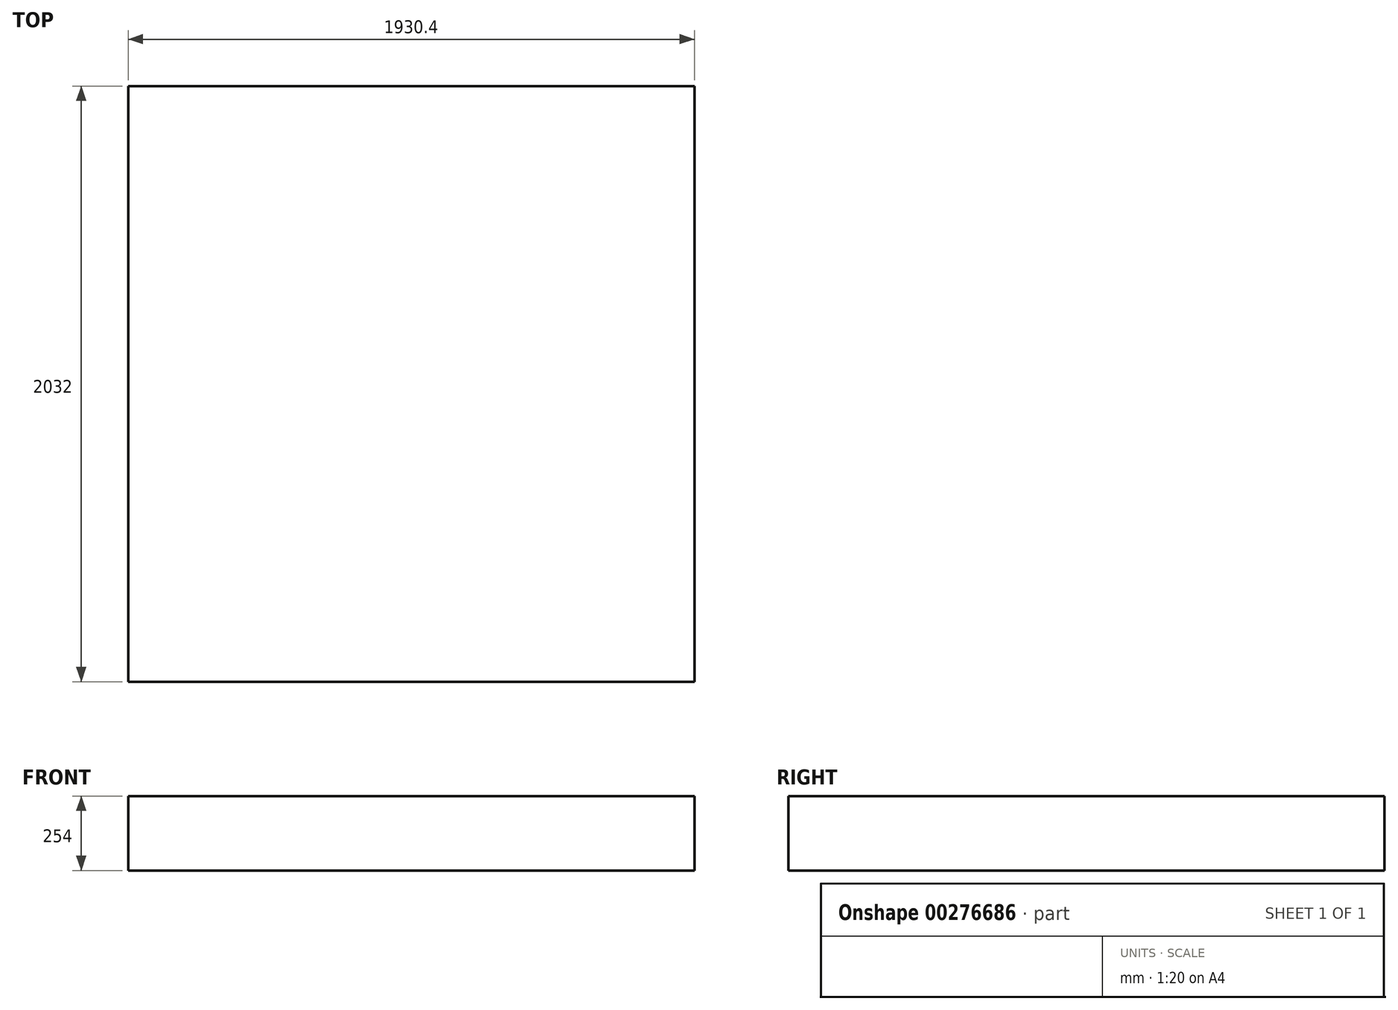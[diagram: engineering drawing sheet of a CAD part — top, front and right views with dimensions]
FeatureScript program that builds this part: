
annotation { "Feature Type Name" : "Feature", "Feature Type Description" : "" }
export const myFeature = defineFeature(function(context is Context, id is Id, definition is map)
    precondition{}
    {
        {
            var Q0;
            Q0=qCreatedBy(makeId("Top.planeOp"),FACE);
            var sketch = newSketch(context, id + "F0", { "sketchPlane" : qUnion([Q0])});
            skLineSegment(sketch, "E0.bottom", {"start": v(979.69, -1126.92) * mm, "end": v(-950.71, -1126.92) * mm});
            skLineSegment(sketch, "E0.top", {"start": v(979.69, 905.08) * mm, "end": v(-950.71, 905.08) * mm});
            skLineSegment(sketch, "E0.left", {"start": v(979.69, -1126.92) * mm, "end": v(979.69, 905.08) * mm});
            skLineSegment(sketch, "E0.right", {"start": v(-950.71, -1126.92) * mm, "end": v(-950.71, 905.08) * mm});
            skSolve(sketch);
        }
        {
            var Q0;
            Q0=makeQuery(id+"F0.imprint","IMPRINT",FACE,{"disambiguationData":[TD([[makeQuery(id+"F0.imprint","IMPRINT",EDGE,{"derivedFrom":sQuery(id+"F0.wireOp",EDGE,"E0.bottom")}),-1.0]])]});
            extrude(context, id + "F1", {"entities" : qUnion([Q0]), "depth" : 254 * mm});
        }
    });
